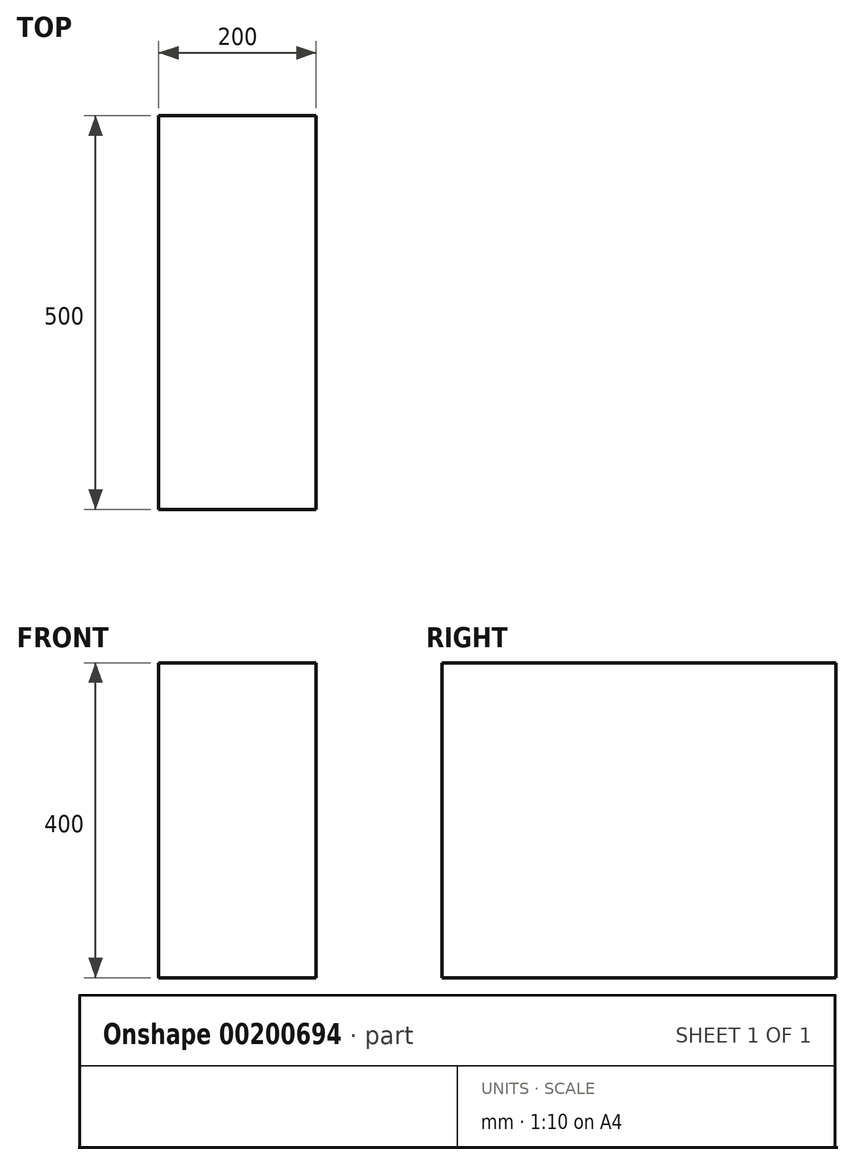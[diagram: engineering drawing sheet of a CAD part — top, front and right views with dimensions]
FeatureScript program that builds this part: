
annotation { "Feature Type Name" : "Feature", "Feature Type Description" : "" }
export const myFeature = defineFeature(function(context is Context, id is Id, definition is map)
    precondition{}
    {
        {
            var Q0;
            Q0=qCreatedBy(makeId("Front.planeOp"),FACE);
            var sketch = newSketch(context, id + "F0", { "sketchPlane" : qUnion([Q0])});
            skLineSegment(sketch, "E0.bottom", {"start": v(0, 0) * mm, "end": v(200, 0) * mm});
            skLineSegment(sketch, "E0.top", {"start": v(0, 400) * mm, "end": v(200, 400) * mm});
            skLineSegment(sketch, "E0.left", {"start": v(0, 0) * mm, "end": v(0, 400) * mm});
            skLineSegment(sketch, "E0.right", {"start": v(200, 0) * mm, "end": v(200, 400) * mm});
            skSolve(sketch);
        }
        {
            var Q0;
            Q0=qSketchRegion(id+"F0",true);
            extrude(context, id + "F1", {"entities" : qUnion([Q0]), "depth" : 500 * mm});
        }
    });
